# Revit family: Building-ContenitoriParete-GEWISS-44CE-CASSETTE-DERIVAZIONE-PARETE_ROTONDE
name_source: partatom
category: Apparecchi elettrici
revit_build: Autodesk Revit 2016 (Build: 20161004_0715(x64)
units: mm (PartAtom-declared; Revit-internal decimal feet)

## family parameters
Condiviso = No
Host = Superficie
Mantenere orientamento annotazione = Sì
Numero OmniClass = 23.80.30.14.24
Punto di calcolo locali = Sì
Quota connettore circolare = Usa diametro
Taglio con vuoti quando caricato = No
Tipo di parte = Normale
Titolo OmniClass = Junction Boxes

## types (1)
- Building-ContenitoriParete-GEWISS-44CE-CASSETTE-DERIVAZIONE-PARETE_ROTONDE
    Accessori per ripristino isolamento = GW44622
    Applicazione = Derivazioni speciali
    Carico apparente = 0 VA
    Catalogo = BUILDING
    Catalogo Serie = 44 CE
    Classe isolamento = II (secondo Norma IEC 61140)
    Classificazione = Other
    Codice EAN = 8011564217720
    Codice Electrocod = 02210
    Colore = Grigio RAL 7035
    Coperchio = Basso a pressione
    Corrugato = <Per categoria>
    Descrizione = CASS.IP44 DIAM.80X40 PASSACAVI GWT 960°C
    Diametro scatola = 80 mm  [stored 0.262467 ft]
    Dim. interne BxHxP (mm) = Ø 80x40
    Elemento di dettaglio = ELEMENTI DI DETTAGLIO 44CE-ROUND : Ø 80x40
    Entrate N. fori / Ã˜ = 4 / 23
    Foro = 42 mm  [stored 0.137795 ft]
    GEWISS SCHEDA TECNICA = http://pro.gewiss.com
    Glow Wire Test = 960°C
    Grado di protezione = IP44
    IDF = a891d691-e4ca-4168-bfca-822674811c97
    IDT = 7d4f1a4b-4295-41f9-b726-f05049c8eb16
    Immagine tipo = GW44001.jpg
    Materiale = Tecnopolimero GWPLAST 75
    Modello = GW44052
    Pareti = Con passacavi
    Produttore = GEWISS S.p.A.
    Prospetto di default = 250 mm
    Raggio = 40 mm  [stored 0.131234 ft]
    Raggio coperchio = 45 mm
    Resistenza agli urti = IK07
    SEO = Cassetta
    Scatola = GEWISS SCATOLA
    Scheda Tecnica = https://www.gewiss.com
    Spessore = 35 mm
    Temperatura di impiego = -25 +60 °C
    Termopressione con biglia = 85 °C
    URL = https://www.gewiss.com
    Versione file RFA = 18.0
    Voltaggio = 0 V
    coperchio scatola = GEWISS COPERCHIO

note: [stored X ft] marks values corroborated as IEEE doubles in the binary element streams (Revit-internal decimal feet)

## geometry (parser evidence)
native form markers: Blend x4, Sweep x1
no freeform markers — native parametric forms only
